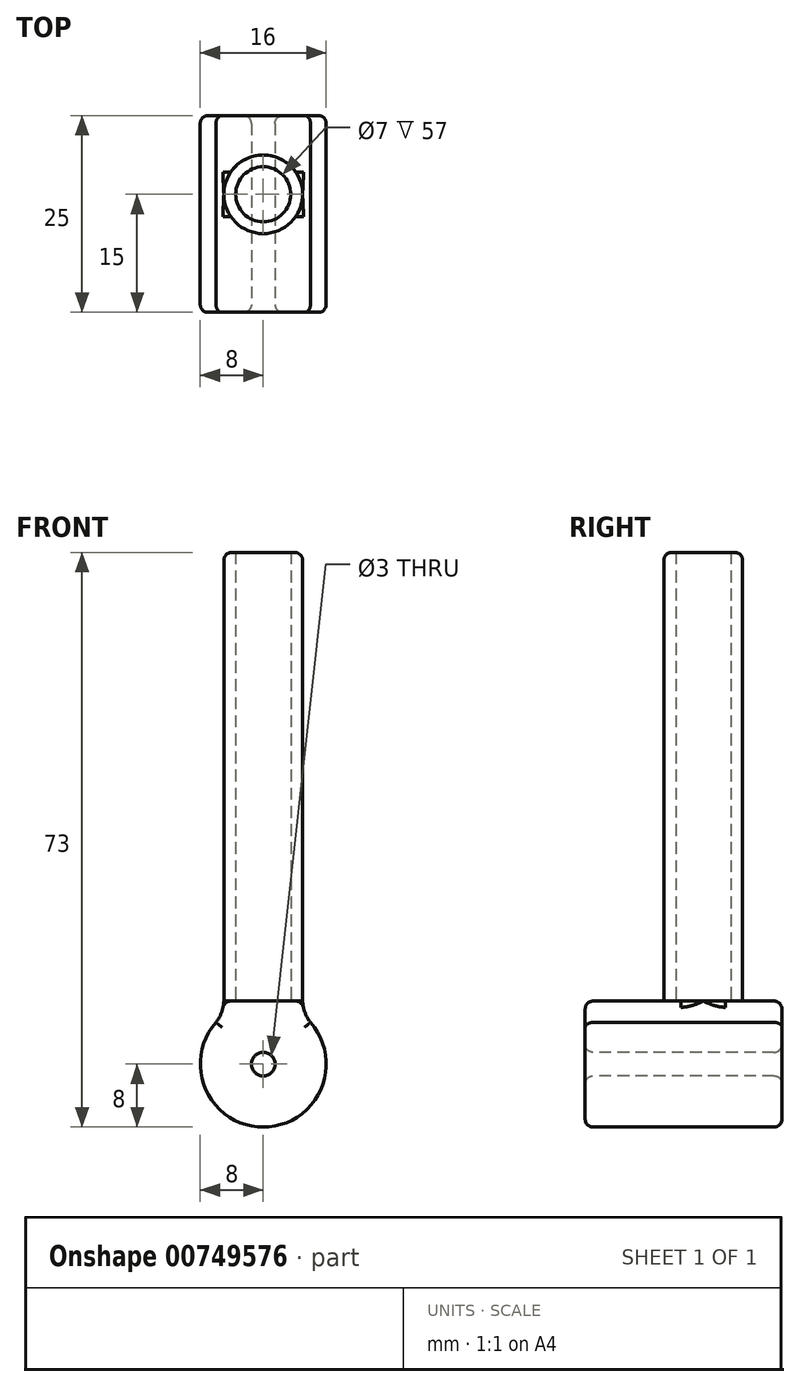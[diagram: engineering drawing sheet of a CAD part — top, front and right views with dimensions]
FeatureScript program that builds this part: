
annotation { "Feature Type Name" : "Feature", "Feature Type Description" : "" }
export const myFeature = defineFeature(function(context is Context, id is Id, definition is map)
    precondition{}
    {
        {
            var Q0;
            Q0=qCreatedBy(makeId("Top.planeOp"),FACE);
            var sketch = newSketch(context, id + "F0", { "sketchPlane" : qUnion([Q0])});
            skCircle(sketch, "E0", {"center": v(0, 0) * mm, "radius": 5 * mm});
            skCircle(sketch, "E1", {"center": v(0, 0) * mm, "radius": 3.5 * mm});
            skLineSegment(sketch, "E2.bottom", {"start": v(-5, 0) * mm, "end": v(5, 0) * mm});
            skSolve(sketch);
        }
        {
            var Q0;
            Q0=makeQuery(id+"F0.imprint","IMPRINT",FACE,{"disambiguationData":[TD([[makeQuery(id+"F0.imprint","IMPRINT",EDGE,{"derivedFrom":sQuery(id+"F0.wireOp",EDGE,"E0")}),1.0]])]});
            extrude(context, id + "F1", {"entities" : qUnion([Q0]), "depth" : 57 * mm, "offsetDistance" : 25 * mm});
        }
        {
            var Q0;
            Q0=qCreatedBy(makeId("Front.planeOp"),FACE);
            var sketch = newSketch(context, id + "F2", { "sketchPlane" : qUnion([Q0])});
            skArc(sketch, "E3", {"start": v(-6, -2.7) * mm, "mid": v(0, -16) * mm, "end": v(6, -2.7) * mm});
            skLineSegment(sketch, "E4", {"start": v(-5, 0) * mm, "end": v(5, 0) * mm});
            skLineSegment(sketch, "E5", {"start": v(-6, -2.7) * mm, "end": v(6, -2.7) * mm, "construction": true});
            skArc(sketch, "E6", {"start": v(-6, -2.7) * mm, "mid": v(-5.3, -1.43) * mm, "end": v(-5, 0) * mm});
            skArc(sketch, "E7.MirrorCS", {"start": v(6, -2.7) * mm, "mid": v(5.3, -1.43) * mm, "end": v(5, 0) * mm});
            skCircle(sketch, "E8", {"center": v(0, -8) * mm, "radius": 1.5 * mm});
            skSolve(sketch);
        }
        {
            var Q0;
            Q0=makeQuery(id+"F2.imprint","IMPRINT",FACE,{"disambiguationData":[TD([[makeQuery(id+"F2.imprint","IMPRINT",EDGE,{"derivedFrom":sQuery(id+"F2.wireOp",EDGE,"E3")}),1.0]])]});
            extrude(context, id + "F3", {"entities" : qUnion([Q0]), "operationType" : NewBodyOperationType.ADD, "oppositeDirection" : true, "depth" : 10 * mm, "offsetDistance" : 25 * mm, "hasSecondDirection" : true, "secondDirectionOppositeDirection" : false, "secondDirectionDepth" : 15 * mm});
        }
        {
            var Q0;
            Q0=makeQuery(id+"F3.opExtrude","CAP_FACE",FACE,{"disambiguationData":[OSD([sQuery(id+"F2.wireOp",EDGE,"E3"),sQuery(id+"F2.wireOp",EDGE,"E4"),sQuery(id+"F2.wireOp",EDGE,"E6"),sQuery(id+"F2.wireOp",EDGE,"E7.MirrorCS"),sQuery(id+"F2.wireOp",EDGE,"E8")])],"isStart":false});
            var Q1;
            Q1=makeQuery(id+"F3.opExtrude","CAP_FACE",FACE,{"disambiguationData":[OSD([sQuery(id+"F2.wireOp",EDGE,"E3"),sQuery(id+"F2.wireOp",EDGE,"E4"),sQuery(id+"F2.wireOp",EDGE,"E6"),sQuery(id+"F2.wireOp",EDGE,"E7.MirrorCS"),sQuery(id+"F2.wireOp",EDGE,"E8")])],"isStart":true});
            var Q2;
            {var subQ0=sQuery(id+"F2.wireOp",EDGE,"E7.MirrorCS");var subQ1=sQuery(id+"F2.wireOp",EDGE,"E4");Q2=makeQuery(id+"F3.boolean.opBoolean","SPLIT",EDGE,{"disambiguationData":[TD([makeQuery(id+"F3.opExtrude","CAP_FACE",FACE,{"disambiguationData":[OSD([sQuery(id+"F2.wireOp",EDGE,"E3"),subQ1,sQuery(id+"F2.wireOp",EDGE,"E6"),subQ0,sQuery(id+"F2.wireOp",EDGE,"E8")])],"isStart":false})])],"derivedFrom":makeQuery(id+"F3.opExtrude","SWEPT_EDGE",EDGE,{"disambiguationData":[OSD([subQ1,subQ0])]})});}
            var Q3;
            {var subQ0=sQuery(id+"F2.wireOp",EDGE,"E6");var subQ1=sQuery(id+"F2.wireOp",EDGE,"E4");Q3=makeQuery(id+"F3.boolean.opBoolean","SPLIT",EDGE,{"disambiguationData":[TD([makeQuery(id+"F3.opExtrude","CAP_FACE",FACE,{"disambiguationData":[OSD([sQuery(id+"F2.wireOp",EDGE,"E3"),subQ1,subQ0,sQuery(id+"F2.wireOp",EDGE,"E7.MirrorCS"),sQuery(id+"F2.wireOp",EDGE,"E8")])],"isStart":false})])],"derivedFrom":makeQuery(id+"F3.opExtrude","SWEPT_EDGE",EDGE,{"disambiguationData":[OSD([subQ1,subQ0])]})});}
            fillet(context, id + "F4", {"entities" : qUnion([Q0, Q1, Q2, Q3]), "radius" : 1 * mm, "tangentPropagation" : true, "allowEdgeOverflow" : false});
        }
        {
            var Q0;
            Q0=makeQuery(id+"F1.opExtrude","CAP_EDGE",EDGE,{"disambiguationData":[OSD([sQuery(id+"F0.wireOp",EDGE,"E0")])],"isStart":false});
            fillet(context, id + "F5", {"entities" : qUnion([Q0]), "radius" : 1 * mm, "tangentPropagation" : true, "allowEdgeOverflow" : false});
        }
    });
